# Revit family: P190780JX-037c_JJD3024HL_Urban_Living_Warming-Drawer
name_source: partatom
category: Specialty Equipment
units: mm (PartAtom-declared; Revit-internal decimal feet)

## family parameters
Always vertical = Yes
Cut with Voids When Loaded = No
Enable Cutting in Views = No
Maintain Annotation Orientation = No
Part Type = Normal
Room Calculation Point = No
Round Connector Dimension = Use Diameter
Shared = No
Work Plane-Based = No

## types (1)
- JJD3024HL
    Amps = 0 A
    Body Material = ARCAT - Metal - Steel - Stainless
    Clearance Material = ARCAT - Clearance
    Default Elevation = 0"
    Depth = 22 3/8"
    Description = JennAir® RISE 24" Warming Drawer
Tiroir-réchaud JennAir® RISE™, 24 po
    Dimension Guide = https://www.whirlpool.com
    Family Name = SMALL SPACES - 24" - Warming Drawer
    Feature 1 = WARMING DRAWER
TIROIR-RÉCHAUD
    Feature 2 = Concealed Controls
Commandes dissimulées
    Feature 3 = Glass-Bottom Drawer Design
Conception de tiroir à fond en verre
    Height = 5 9/16"
    Installation-Fabrication = https://www.whirlpool.com
    Leg Material = ARCAT - Plastic - Black
    Manufacturer = JennAir
    Model = JJD3024HL
    Voltage = 0 V
    Width = 23 7/16"

## geometry (parser evidence)
native form markers: Sweep x3
no freeform markers — native parametric forms only
